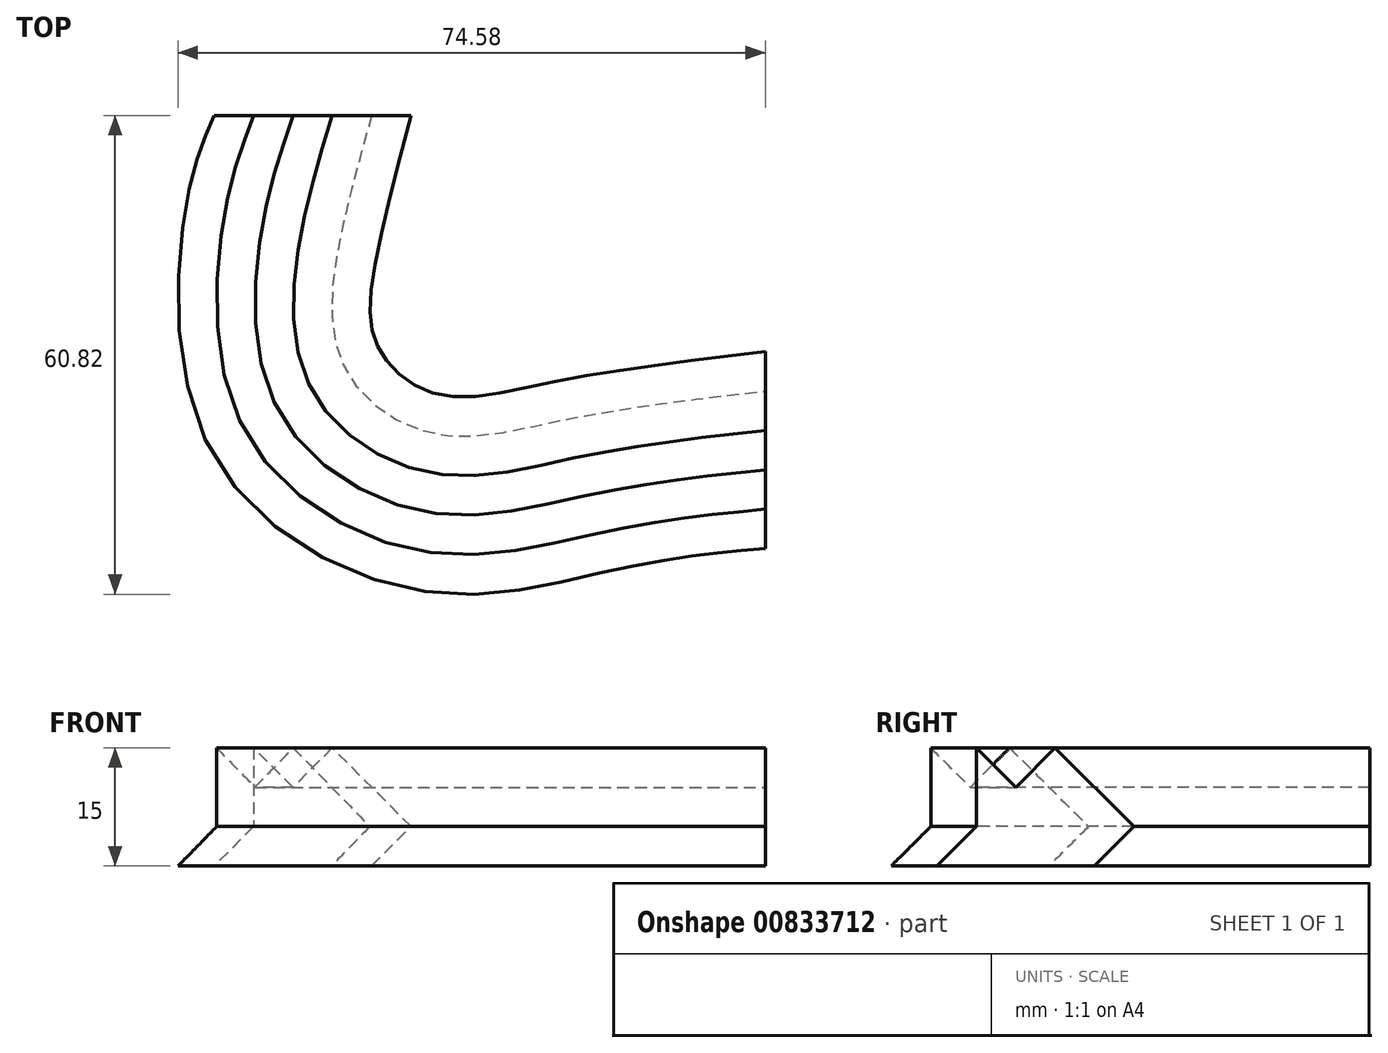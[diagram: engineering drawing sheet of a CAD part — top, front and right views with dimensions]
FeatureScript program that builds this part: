
annotation { "Feature Type Name" : "Feature", "Feature Type Description" : "" }
export const myFeature = defineFeature(function(context is Context, id is Id, definition is map)
    precondition{}
    {
        {
            var Q0;
            Q0=qCreatedBy(makeId("Front.planeOp"),FACE);
            var sketch = newSketch(context, id + "F0", { "sketchPlane" : qUnion([Q0])});
            skLineSegment(sketch, "E0", {"start": v(-70, 0) * mm, "end": v(-50, 0) * mm});
            skLineSegment(sketch, "E1", {"start": v(-50, 0) * mm, "end": v(-45, 5) * mm});
            skLineSegment(sketch, "E2", {"start": v(-45, 5) * mm, "end": v(-55, 15) * mm});
            skLineSegment(sketch, "E3", {"start": v(-55, 15) * mm, "end": v(-60, 10) * mm});
            skLineSegment(sketch, "E4", {"start": v(-60, 10) * mm, "end": v(-65, 15) * mm});
            skLineSegment(sketch, "E5", {"start": v(-65, 15) * mm, "end": v(-65, 5) * mm});
            skLineSegment(sketch, "E6", {"start": v(-65, 5) * mm, "end": v(-70, 0) * mm});
            skLineSegment(sketch, "E7", {"start": v(-70, 0) * mm, "end": v(-55, 15) * mm, "construction": true});
            skSolve(sketch);
        }
        {
            var Q0;
            Q0=qCreatedBy(makeId("Right.planeOp"),FACE);
            var sketch = newSketch(context, id + "F1", { "sketchPlane" : qUnion([Q0])});
            skLineSegment(sketch, "E8", {"start": v(-55, 0) * mm, "end": v(-35, 0) * mm});
            skLineSegment(sketch, "E9", {"start": v(-35, 0) * mm, "end": v(-30, 5) * mm});
            skLineSegment(sketch, "E10", {"start": v(-30, 5) * mm, "end": v(-40, 15) * mm});
            skLineSegment(sketch, "E11", {"start": v(-40, 15) * mm, "end": v(-45, 10) * mm});
            skLineSegment(sketch, "E12", {"start": v(-45, 10) * mm, "end": v(-50, 15) * mm});
            skLineSegment(sketch, "E13", {"start": v(-50, 15) * mm, "end": v(-50, 5) * mm});
            skLineSegment(sketch, "E14", {"start": v(-50, 5) * mm, "end": v(-55, 0) * mm});
            skLineSegment(sketch, "E15", {"start": v(-55, 0) * mm, "end": v(-40, 15) * mm, "construction": true});
            skSolve(sketch);
        }
        {
            var Q0;
            Q0=qCreatedBy(makeId("Top.planeOp"),FACE);
            var sketch = newSketch(context, id + "F2", { "sketchPlane" : qUnion([Q0])});
            skFitSpline(sketch, "E16", {"points": [v(-50, 0) * mm, v(-55.13, -27.34) * mm, v(-41.08, -40.59) * mm, v(0, -35) * mm], "startDerivative": vector(-2.4, -56.64) * mm, "endDerivative": vector(174.43, 6.02) * mm});
            skFitSpline(sketch, "E17", {"points": [v(-70, 0) * mm, v(-86.26, -36.98) * mm, v(-59.93, -67.3) * mm, v(0, -55) * mm], "startDerivative": vector(-4.09, -67.49) * mm, "endDerivative": vector(192.13, 27.19) * mm});
            skSolve(sketch);
        }
        {
            var Q0;
            Q0=sQuery(id+"F2.wireOp",EDGE,"E16");
            var Q1;
            Q1=makeQuery(id+"F0.imprint","IMPRINT",FACE,{"disambiguationData":[TD([[makeQuery(id+"F0.imprint","IMPRINT",EDGE,{"derivedFrom":sQuery(id+"F0.wireOp",EDGE,"E0")}),1.0]])]});
            var Q2;
            Q2=makeQuery(id+"F1.imprint","IMPRINT",FACE,{"disambiguationData":[TD([[makeQuery(id+"F1.imprint","IMPRINT",EDGE,{"derivedFrom":sQuery(id+"F1.wireOp",EDGE,"E8")}),1.0]])]});
            var Q3;
            Q3=sQuery(id+"F2.wireOp",EDGE,"E16");
            var Q4;
            Q4=sQuery(id+"F2.wireOp",EDGE,"E17");
            loft(context, id + "F3", {"addSections" : true, "spine" : qUnion([Q0]), "sectionCount" : 4, "sheetProfilesArray" : [{ "sheetProfileEntities" : qUnion([Q1]) }, { "sheetProfileEntities" : qUnion([Q2]) }], "guidesArray" : [{ "guideEntities" : qUnion([Q3]), "guideDerivativeType" : LoftGuideDerivativeType.DEFAULT, "guideDerivativeMagnitude" : 1 }, { "guideEntities" : qUnion([Q4]), "guideDerivativeType" : LoftGuideDerivativeType.DEFAULT, "guideDerivativeMagnitude" : 1 }]});
        }
    });
